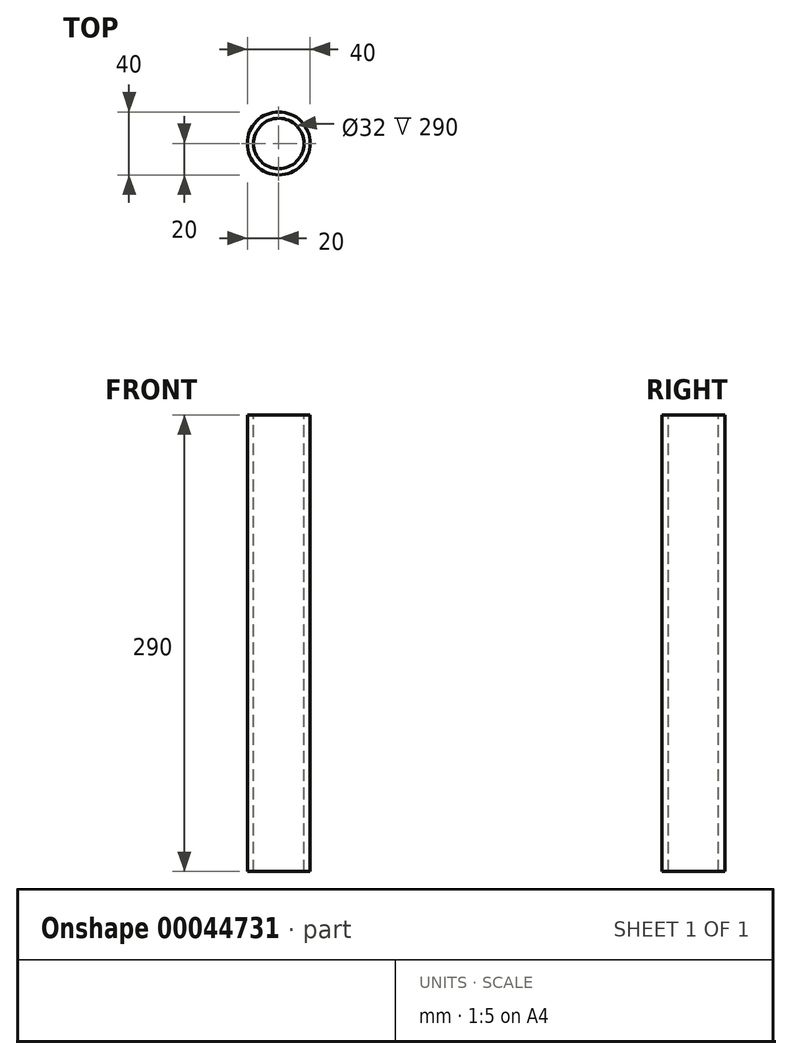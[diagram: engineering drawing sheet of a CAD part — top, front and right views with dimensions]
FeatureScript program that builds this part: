
annotation { "Feature Type Name" : "Feature", "Feature Type Description" : "" }
export const myFeature = defineFeature(function(context is Context, id is Id, definition is map)
    precondition{}
    {
        {
            var Q0;
            Q0=qCreatedBy(makeId("Top.planeOp"),FACE);
            var sketch = newSketch(context, id + "F0", { "sketchPlane" : qUnion([Q0])});
            skCircle(sketch, "E0", {"center": v(0, 0) * mm, "radius": 20 * mm});
            skSolve(sketch);
        }
        {
            var Q0;
            Q0 = qSketchRegion(id + "F0", true);
            extrude(context, id + "F1", {"entities" : qUnion([Q0]), "depth" : 290 * mm});
        }
        {
            var Q0;
            Q0=makeQuery(id+"F1.opExtrude","CAP_FACE",FACE,{"disambiguationData":[OSD([sQuery(id+"F0.wireOp",EDGE,"E0")])],"isStart":false});
            var sketch = newSketch(context, id + "F2", { "sketchPlane" : qUnion([Q0])});
            skCircle(sketch, "E1", {"center": v(0, 0) * mm, "radius": 16 * mm});
            skSolve(sketch);
        }
        {
            var Q0;
            Q0=sQuery(id+"F2.wireOp",VERTEX,"E1.center");
            var Q1;
            Q1=makeQuery(id+"F1.opExtrude","SWEPT_BODY",BODY,{"disambiguationData":[OSD([sQuery(id+"F0.wireOp",EDGE,"E0")])]});
            hole(context, id + "F3", {"style" : HoleStyle.SIMPLE, "holeDiameter" : 32 * mm, "endStyle" : HoleEndStyle.THROUGH, "locations" : qUnion([Q0]), "scope" : qUnion([Q1]), "isTappedThrough" : true});
        }
    });
